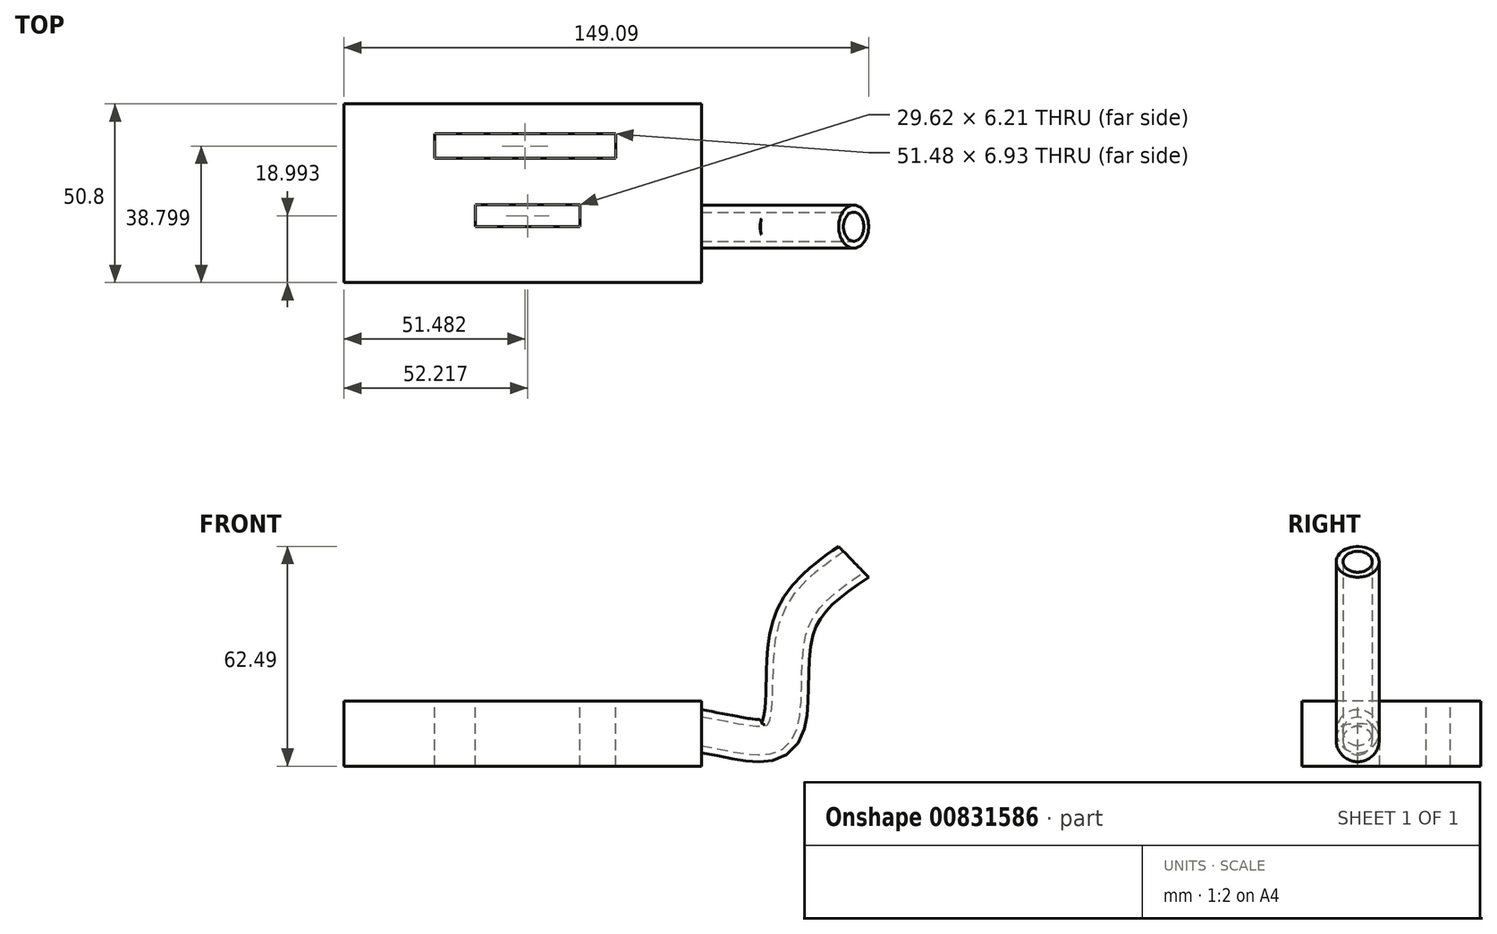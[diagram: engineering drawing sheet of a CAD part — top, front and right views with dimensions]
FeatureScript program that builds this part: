
annotation { "Feature Type Name" : "Feature", "Feature Type Description" : "" }
export const myFeature = defineFeature(function(context is Context, id is Id, definition is map)
    precondition{}
    {
        {
            var Q0;
            Q0=qCreatedBy(makeId("Top.planeOp"),FACE);
            var sketch = newSketch(context, id + "F0", { "sketchPlane" : qUnion([Q0])});
            skLineSegment(sketch, "E0.bottom", {"start": v(-77.22, 34.91) * mm, "end": v(24.38, 34.91) * mm});
            skLineSegment(sketch, "E0.top", {"start": v(-77.22, -15.89) * mm, "end": v(24.38, -15.89) * mm});
            skLineSegment(sketch, "E0.left", {"start": v(-77.22, 34.91) * mm, "end": v(-77.22, -15.89) * mm});
            skLineSegment(sketch, "E0.right", {"start": v(24.38, 34.91) * mm, "end": v(24.38, -15.89) * mm});
            skSolve(sketch);
        }
        {
            var Q0;
            Q0=makeQuery(id+"F0.imprint","IMPRINT",FACE,{"disambiguationData":[TD([[makeQuery(id+"F0.imprint","IMPRINT",EDGE,{"derivedFrom":sQuery(id+"F0.wireOp",EDGE,"E0.bottom")}),-1.0]])]});
            extrude(context, id + "F1", {"entities" : qUnion([Q0]), "depth" : 18.54 * mm, "offsetDistance" : 25.4 * mm});
        }
        {
            var Q0;
            Q0=makeQuery(id+"F1.opExtrude","CAP_FACE",FACE,{"disambiguationData":[OSD([sQuery(id+"F0.wireOp",EDGE,"E0.bottom"),sQuery(id+"F0.wireOp",EDGE,"E0.top"),sQuery(id+"F0.wireOp",EDGE,"E0.left"),sQuery(id+"F0.wireOp",EDGE,"E0.right")])],"isStart":false});
            var sketch = newSketch(context, id + "F2", { "sketchPlane" : qUnion([Q0])});
            skLineSegment(sketch, "E1.bottom", {"start": v(-10.2, 6.2) * mm, "end": v(-39.82, 6.2) * mm});
            skLineSegment(sketch, "E1.top", {"start": v(-10.2, 0) * mm, "end": v(-39.82, 0) * mm});
            skLineSegment(sketch, "E1.left", {"start": v(-10.2, 6.2) * mm, "end": v(-10.2, 0) * mm});
            skLineSegment(sketch, "E1.right", {"start": v(-39.82, 6.2) * mm, "end": v(-39.82, 0) * mm});
            skLineSegment(sketch, "E2.bottom", {"start": v(0, 26.38) * mm, "end": v(-51.48, 26.38) * mm});
            skLineSegment(sketch, "E2.top", {"start": v(0, 19.44) * mm, "end": v(-51.48, 19.44) * mm});
            skLineSegment(sketch, "E2.left", {"start": v(0, 26.38) * mm, "end": v(0, 19.44) * mm});
            skLineSegment(sketch, "E2.right", {"start": v(-51.48, 26.38) * mm, "end": v(-51.48, 19.44) * mm});
            skSolve(sketch);
        }
        {
            var Q0;
            Q0=makeQuery(id+"F2.imprint","IMPRINT",FACE,{"disambiguationData":[TD([[makeQuery(id+"F2.imprint","IMPRINT",EDGE,{"derivedFrom":sQuery(id+"F2.wireOp",EDGE,"E2.bottom")}),1.0]])]});
            var Q1;
            Q1=makeQuery(id+"F2.imprint","IMPRINT",FACE,{"disambiguationData":[TD([[makeQuery(id+"F2.imprint","IMPRINT",EDGE,{"derivedFrom":sQuery(id+"F2.wireOp",EDGE,"E1.bottom")}),1.0]])]});
            extrude(context, id + "F3", {"entities" : qUnion([Q0, Q1]), "operationType" : NewBodyOperationType.REMOVE, "oppositeDirection" : true, "depth" : 25.4 * mm, "offsetDistance" : 25.4 * mm});
        }
        {
            var Q0;
            Q0=qCreatedBy(makeId("Front.planeOp"),FACE);
            var sketch = newSketch(context, id + "F4", { "sketchPlane" : qUnion([Q0])});
            skFitSpline(sketch, "E3", {"points": [v(24.37, 9.85) * mm, v(46.7, 9.65) * mm, v(50.21, 38.46) * mm, v(67.67, 58.04) * mm], "startDerivative": vector(111.5, -19.2) * mm, "endDerivative": vector(71.44, 49.08) * mm});
            skSolve(sketch);
        }
        {
            var Q0;
            Q0=makeQuery(id+"F1.opExtrude","SWEPT_FACE",FACE,{"disambiguationData":[OSD([sQuery(id+"F0.wireOp",EDGE,"E0.right")])]});
            var sketch = newSketch(context, id + "F5", { "sketchPlane" : qUnion([Q0])});
            skCircle(sketch, "E4", {"center": v(0, 9.94) * mm, "radius": 6.11 * mm});
            skCircle(sketch, "E5", {"center": v(0, 9.94) * mm, "radius": 4.14 * mm});
            skSolve(sketch);
        }
        {
            var Q0;
            Q0=makeQuery(id+"F5.imprint","IMPRINT",FACE,{"disambiguationData":[TD([[makeQuery(id+"F5.imprint","IMPRINT",EDGE,{"derivedFrom":sQuery(id+"F5.wireOp",EDGE,"E4")}),1.0]])]});
            var Q1;
            Q1=sQuery(id+"F4.wireOp",EDGE,"E3");
            sweep(context, id + "F6", {"operationType" : NewBodyOperationType.ADD, "profiles" : qUnion([Q0]), "path" : qUnion([Q1])});
        }
    });
